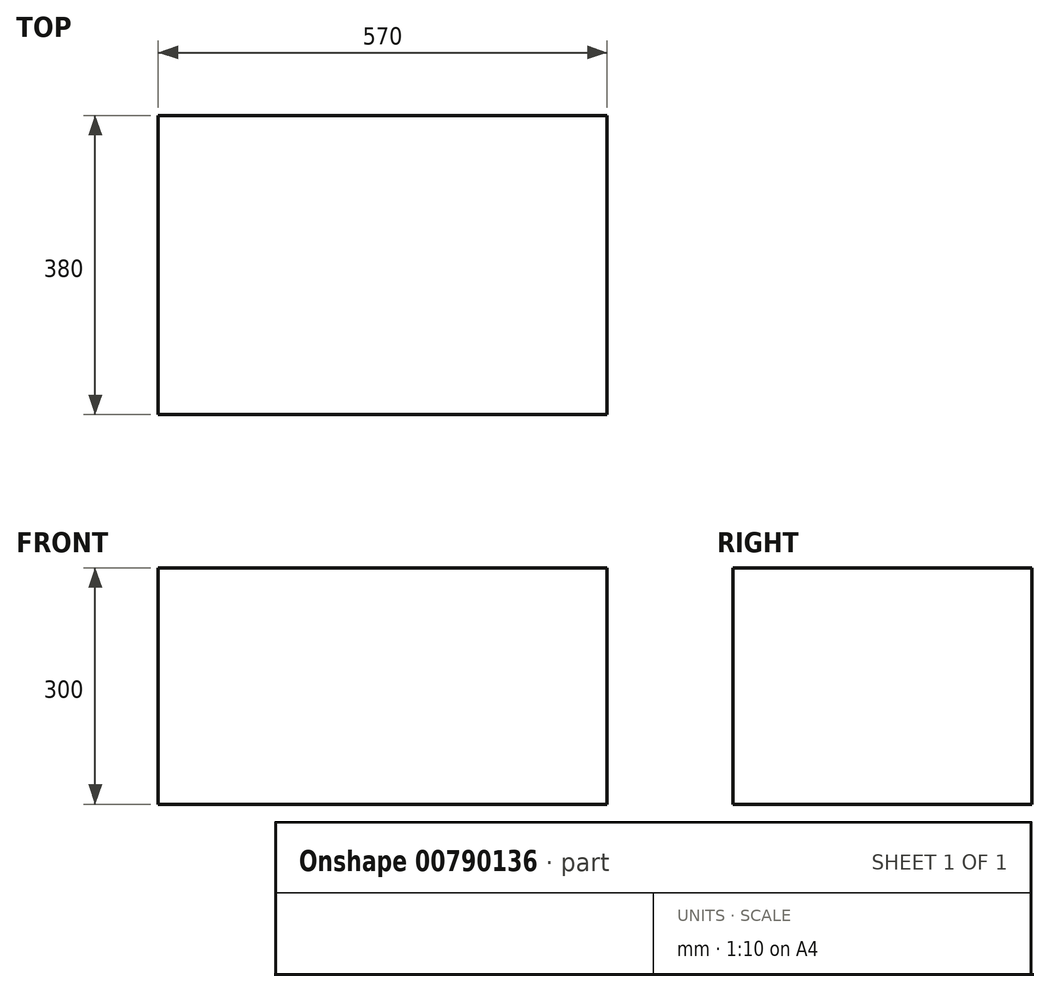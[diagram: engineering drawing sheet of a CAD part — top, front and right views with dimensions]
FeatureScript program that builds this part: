
annotation { "Feature Type Name" : "Feature", "Feature Type Description" : "" }
export const myFeature = defineFeature(function(context is Context, id is Id, definition is map)
    precondition{}
    {
        {
            var Q0;
            Q0=qCreatedBy(makeId("Right.planeOp"),FACE);
            var sketch = newSketch(context, id + "F0", { "sketchPlane" : qUnion([Q0])});
            skLineSegment(sketch, "E0.bottom", {"start": v(190, 150) * mm, "end": v(-190, 150) * mm});
            skLineSegment(sketch, "E0.top", {"start": v(190, -150) * mm, "end": v(-190, -150) * mm});
            skLineSegment(sketch, "E0.left", {"start": v(190, 150) * mm, "end": v(190, -150) * mm});
            skLineSegment(sketch, "E0.right", {"start": v(-190, 150) * mm, "end": v(-190, -150) * mm});
            skPoint(sketch, "E0.middle", {"position": v(0, 0) * mm});
            skSolve(sketch);
        }
        {
            var Q0;
            Q0 = qSketchRegion(id + "F0", true);
            extrude(context, id + "F1", {"entities" : qUnion([Q0]), "depth" : 570 * mm, "offsetDistance" : 25 * mm});
        }
    });
